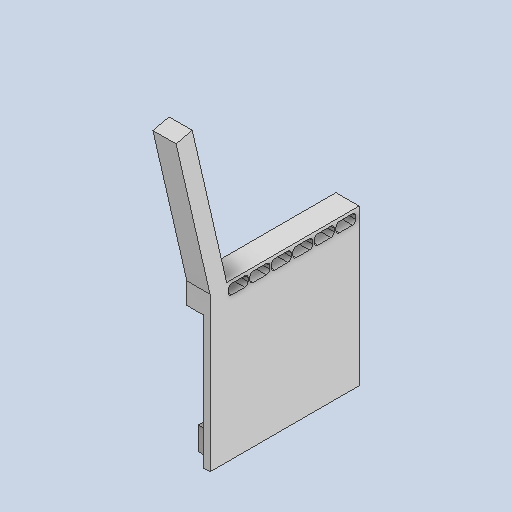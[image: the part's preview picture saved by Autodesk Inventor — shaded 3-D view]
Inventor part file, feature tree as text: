
AUTODESK INVENTOR PART (.ipt)
format: ipt  version: 2023 (Build 270158030, 158C)  size: 210,432 bytes
history: native  units: mm
features: sketch x4, other x3
ambient origin geometry x8: Origin, YZ Plane, XZ Plane, XY Plane, X Axis, Y Axis, Z Axis, Center Point
bodies: Solid1 (feature_tree)
feature tree (7):
  other  "bench-end-peice.ipt"
  other  "Solid1::bench-end-peice.ipt"
  other  "TaggingFeature1"
  sketch  "Sketch1"  dims[d0=10.0mm]
  sketch  "Sketch2"
  sketch  "Sketch3"
  sketch  "Sketch4"
